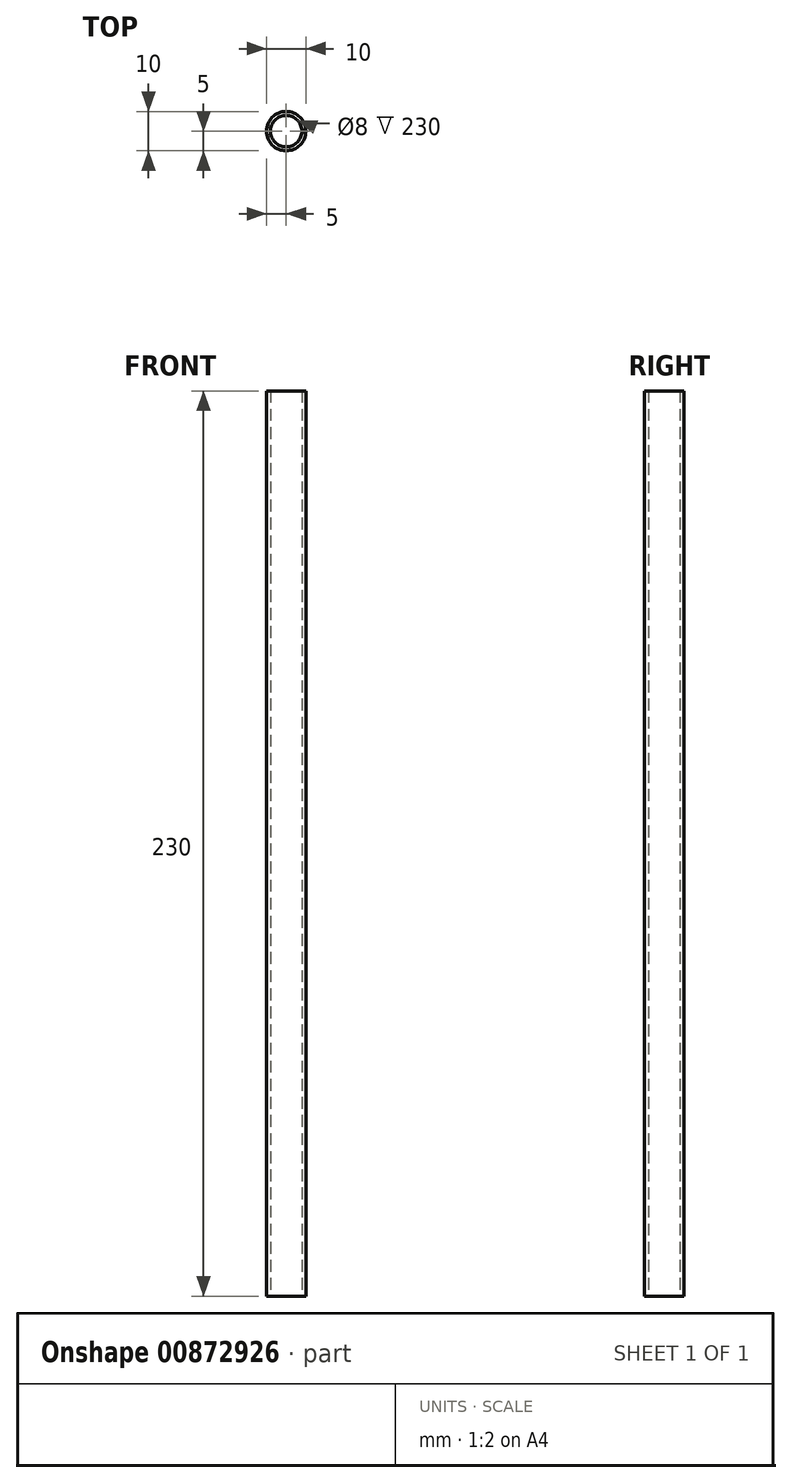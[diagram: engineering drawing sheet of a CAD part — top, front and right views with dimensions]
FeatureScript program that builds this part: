
annotation { "Feature Type Name" : "Feature", "Feature Type Description" : "" }
export const myFeature = defineFeature(function(context is Context, id is Id, definition is map)
    precondition{}
    {
        {
            var Q0;
            Q0=qCreatedBy(makeId("Top.planeOp"),FACE);
            var sketch = newSketch(context, id + "F0", { "sketchPlane" : qUnion([Q0])});
            skCircle(sketch, "E0", {"center": v(0, 0) * mm, "radius": 4 * mm});
            skCircle(sketch, "E1", {"center": v(0, 0) * mm, "radius": 5 * mm});
            skSolve(sketch);
        }
        {
            var Q0;
            Q0=qSketchRegion(id+"F0",true);
            extrude(context, id + "F1", {"entities" : qUnion([Q0]), "endBound" : BoundingType.SYMMETRIC, "depth" : 230 * mm, "offsetDistance" : 25 * mm});
        }
    });
